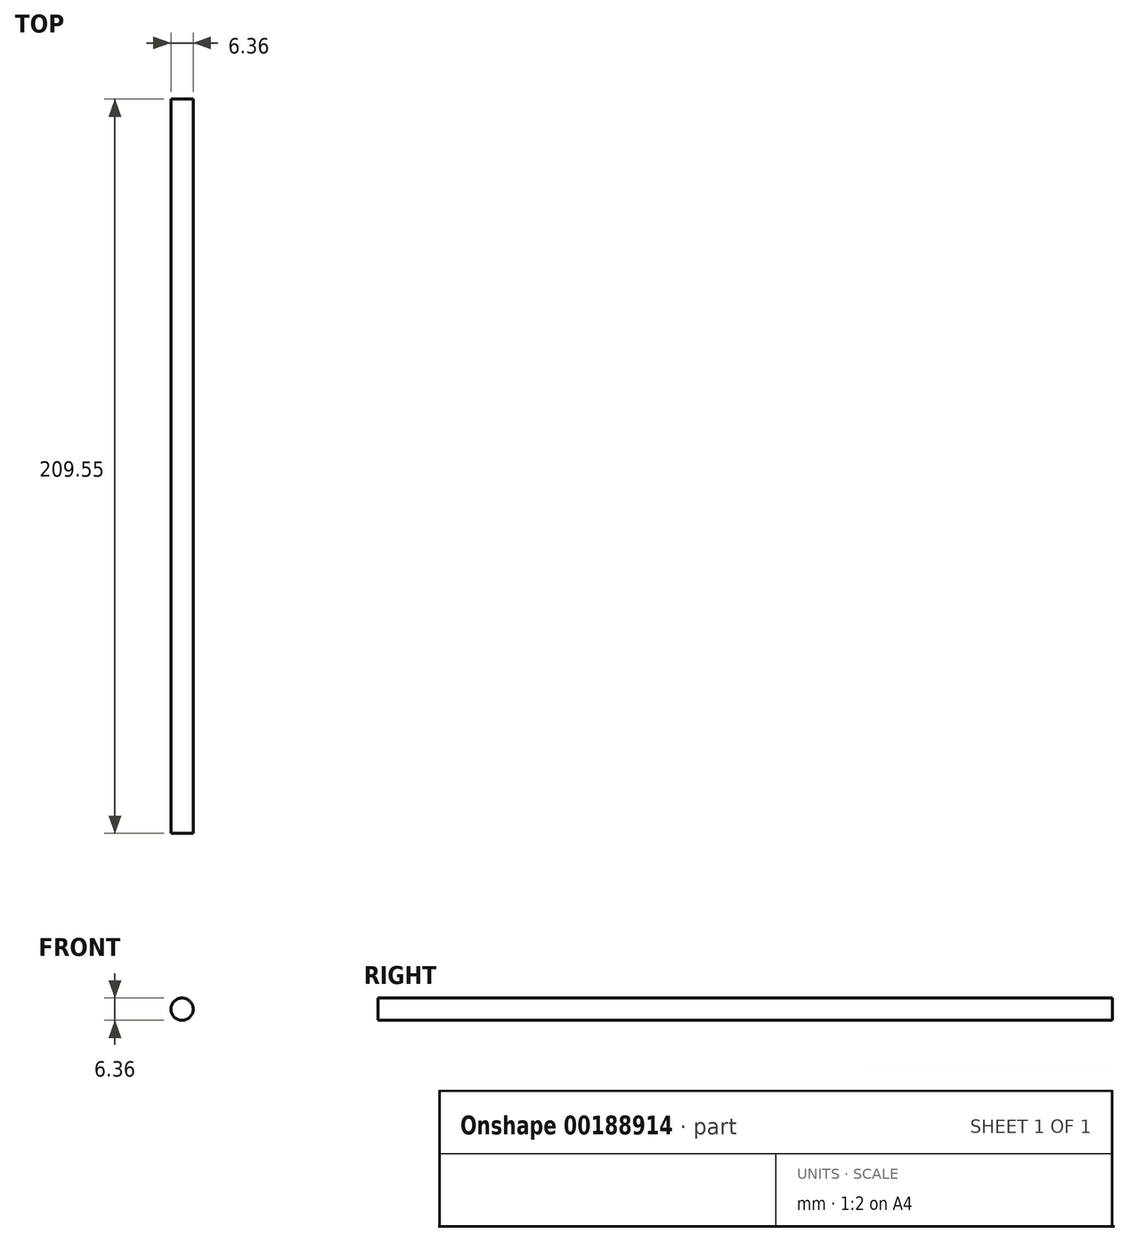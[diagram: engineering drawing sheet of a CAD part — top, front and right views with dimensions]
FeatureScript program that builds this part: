
annotation { "Feature Type Name" : "Feature", "Feature Type Description" : "" }
export const myFeature = defineFeature(function(context is Context, id is Id, definition is map)
    precondition{}
    {
        {
            var Q0;
            Q0=qCreatedBy(makeId("Front.planeOp"),FACE);
            var sketch = newSketch(context, id + "F0", { "sketchPlane" : qUnion([Q0])});
            skCircle(sketch, "E0", {"center": v(0, 0) * mm, "radius": 3.18 * mm});
            skSolve(sketch);
        }
        {
            var Q0;
            Q0=qSketchRegion(id+"F0",true);
            extrude(context, id + "F1", {"entities" : qUnion([Q0]), "depth" : 209.55 * mm});
        }
    });
